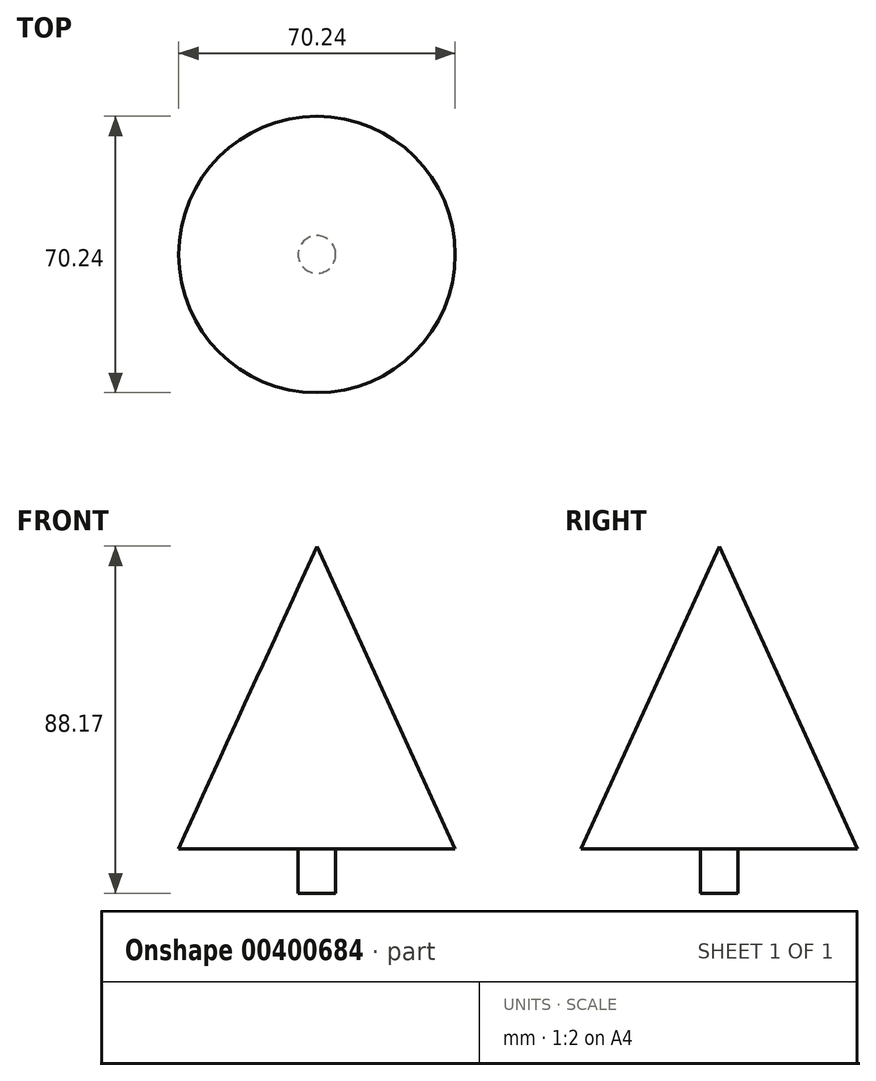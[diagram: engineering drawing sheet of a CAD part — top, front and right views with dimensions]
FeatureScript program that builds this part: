
annotation { "Feature Type Name" : "Feature", "Feature Type Description" : "" }
export const myFeature = defineFeature(function(context is Context, id is Id, definition is map)
    precondition{}
    {
        {
            var Q0;
            Q0=qCreatedBy(makeId("Front.planeOp"),FACE);
            var sketch = newSketch(context, id + "F0", { "sketchPlane" : qUnion([Q0])});
            skLineSegment(sketch, "E0", {"start": v(0, 69.73) * mm, "end": v(0, -37.63) * mm});
            skLineSegment(sketch, "E1", {"start": v(0, -37.63) * mm, "end": v(4.77, -37.63) * mm});
            skLineSegment(sketch, "E2", {"start": v(4.77, -37.63) * mm, "end": v(4.77, -26.32) * mm});
            skLineSegment(sketch, "E3", {"start": v(4.77, -26.32) * mm, "end": v(35.12, -26.32) * mm});
            skLineSegment(sketch, "E4", {"start": v(35.12, -26.32) * mm, "end": v(0, 50.54) * mm});
            skSolve(sketch);
        }
        {
            var Q0;
            Q0 = qSketchRegion(id + "F0", true);
            var Q1;
            Q1=sQuery(id+"F0.wireOp",EDGE,"E0");
            revolve(context, id + "F1", {"entities" : qUnion([Q0]), "axis" : qUnion([Q1]), "revolveType" : RevolveType.FULL});
        }
        {
            var Q0;
            Q0 = qSketchRegion(id + "F0", true);
            var Q1;
            Q1=sQuery(id+"F0.wireOp",EDGE,"E0");
            revolve(context, id + "F2", {"entities" : qUnion([Q0]), "axis" : qUnion([Q1]), "revolveType" : RevolveType.FULL});
        }
    });
